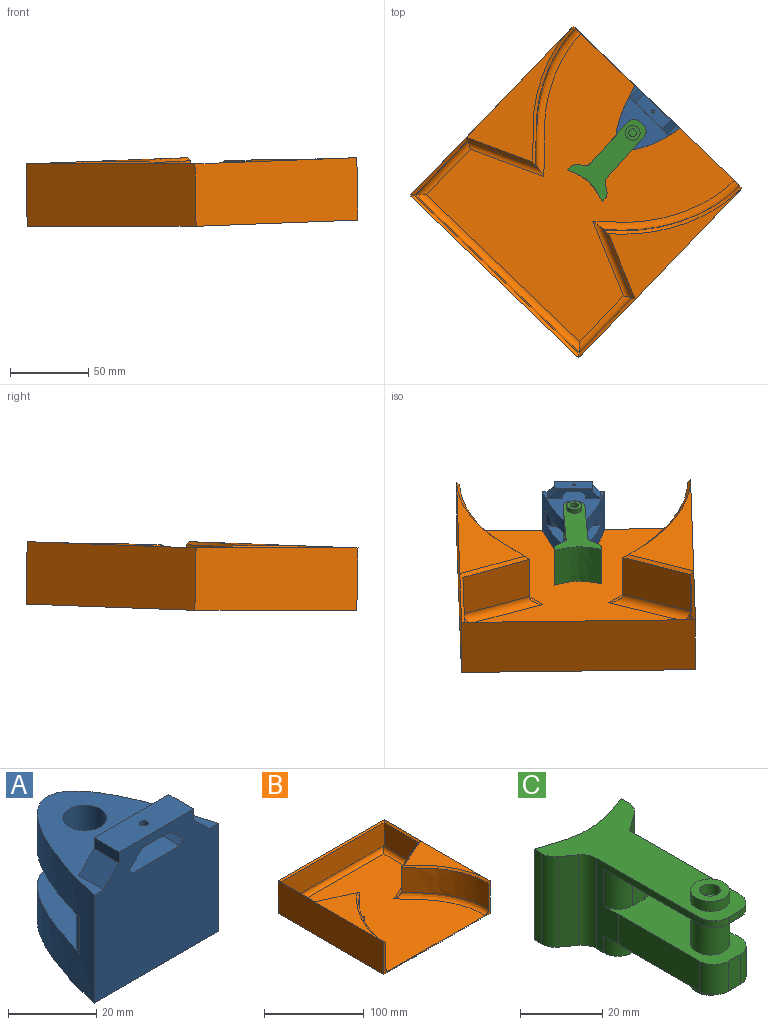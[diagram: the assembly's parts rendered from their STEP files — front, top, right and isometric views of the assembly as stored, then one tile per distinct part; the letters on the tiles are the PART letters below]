
ASSEMBLY  parts=3 mates=2
PART A: 24 faces, bbox 40x36.5x38 mm
  f0: plane 34x8mm, normal (0,1,0), area 140.4mm2, adj f1,f11,f12,f13,f14,f16,f17,f20
  f1: plane 40x36.51mm, normal (0,0,1), area 724.5mm2, adj f0,f2,f3,f10,f16,f17,f22,f23
  f2: extruded ~40x35mm, area 1821.4mm2, adj f1,f3,f4,f6,f7,f18,f19
  f3: plane 40x38mm, normal (0,-1,0), area 1340.4mm2, adj f1,f2,f4,f11,f12,f13,f14,f16
  f4: plane 40x36.51mm, normal (0,0,-1), area 955.1mm2, adj f2,f3
  f5: plane 26.97x10mm, normal (0,1,0), area 269.7mm2, adj f6,f7,f18,f19
  f6: plane 36.58x28.72mm, normal (0,0,-1), area 508.6mm2, adj f2,f5,f10,f18,f19
  f7: plane 36.58x28.72mm, normal (0,0,1), area 508.6mm2, adj f2,f5,f8,f18,f19
  f8: cylinder r=5mm len=10mm, axis (0,0,1), area 157.1mm2, adj f7,f9
  f9: cone r=0mm half-angle=59deg, axis (0,0,1), area 91.6mm2, adj f8
  f10: cylinder r=5mm len=10mm, axis (0,0,1), area 314.2mm2, adj f1,f6
  f11: plane 8x3mm, normal (-1,0,0), area 24mm2, adj f0,f3,f13,f23
  f12: plane 8x3mm, normal (1,0,0), area 24mm2, adj f0,f3,f13,f22
  f13: plane 24x8mm, normal (0,0,1), area 188.9mm2, adj f0,f3,f11,f12,f15
  f14: plane 9x8mm, normal (0,0,-1), area 68.9mm2, adj f0,f3,f15,f20,f21
  f15: cylinder r=1mm len=2.5mm, axis (0,0,1), area 15.7mm2, adj f13,f14
  f16: plane 8x1.25mm, normal (-0.71,0,0.71), area 14.1mm2, adj f0,f1,f3,f20
  f17: plane 8x1.25mm, normal (0.71,0,0.71), area 14.1mm2, adj f0,f1,f3,f21
  f18: cylinder r=5mm len=10mm, axis (0,0,-1), area 63.6mm2, adj f2,f5,f6,f7
  f19: cylinder r=5mm len=10mm, axis (0,0,-1), area 65.5mm2, adj f2,f5,f6,f7
  f20: plane 8x4.25mm, normal (-0.71,0,-0.71), area 48.1mm2, adj f0,f3,f14,f16
  f21: plane 8x4.25mm, normal (0.71,0,-0.71), area 48.1mm2, adj f0,f3,f14,f17
  f22: plane 8x5mm, normal (0.71,0,0.71), area 56.6mm2, adj f0,f1,f3,f12
  f23: plane 8x5mm, normal (-0.71,0,0.71), area 56.6mm2, adj f0,f1,f3,f11
PART B: 29 faces, bbox 152.7x155.3x42.7 mm
  f0: plane 100.52x44.36mm, normal (0,0,1), area 1461.1mm2, adj f2,f17,f19
  f1: extruded ~80.59x43mm, area 2909.3mm2, adj f5,f11,f17,f27,f28
  f2: plane 150x40mm, normal (1,0,0), area 6000mm2, adj f0,f3,f5,f13,f21
  f3: plane 150x40mm, normal (0,1,0), area 6000mm2, adj f2,f4,f13,f20
  f4: plane 150x40mm, normal (-1,0,0), area 6000mm2, adj f3,f5,f12,f13,f18
  f5: plane 150x40mm, normal (0,-1,0), area 312.7mm2, adj f1,f2,f4,f6,f13,f14,f15,f17
  f6: extruded ~79.99x43mm, area 2895.3mm2, adj f5,f7,f15,f22,f23
  f7: plane 43x29.74mm, normal (0.41,0.91,0), area 1387.6mm2, adj f6,f8,f16,f23
  f8: plane 48.91x29.36mm, normal (1,0,0), area 1403.8mm2, adj f7,f9,f18,f23,f24
  f9: plane 146x28.19mm, normal (0,-1,0), area 4115mm2, adj f8,f10,f20,f24,f25,f26
  f10: plane 48.86x29.35mm, normal (-1,0,0), area 1402.5mm2, adj f9,f11,f21,f26,f27
  f11: plane 43x29.73mm, normal (-0.4,0.92,0), area 1380.5mm2, adj f1,f10,f19,f27
  f12: plane 98.48x42.02mm, normal (0,0,1), area 1448.7mm2, adj f4,f15,f16
  f13: plane 150x150mm, normal (0,0,-1), area 22500mm2, adj f2,f3,f4,f5
  f14: plane 143.14x136mm, normal (0,-0.03,1), area 15961.1mm2, adj f5,f22,f23,f24,f25,f26,f27,f28
  f15: bspline ~87.22x48.6mm, area 262.9mm2, adj f5,f6,f12,f16
  f16: plane 45.01x19.68mm, normal (0.29,0.65,0.71), area 130.5mm2, adj f7,f12,f15,f18
  f17: bspline ~86.45x46.7mm, area 264.3mm2, adj f0,f1,f5,f19
  f18: plane 52.21x2mm, normal (0.71,0,0.71), area 143mm2, adj f4,f8,f16,f20
  f19: plane 45.14x19.43mm, normal (-0.28,0.65,0.71), area 130.4mm2, adj f0,f11,f17,f21
  f20: plane 150x2mm, normal (0,-0.71,0.71), area 418.6mm2, adj f3,f9,f18,f21
  f21: plane 52.18x2mm, normal (-0.71,0,0.71), area 142.9mm2, adj f2,f10,f19,f20
  f22: bspline ~126.16x98.33mm, area 740.9mm2, adj f5,f6,f14,f23
  f23: cylinder r=5mm len=52.2mm, axis (-0.91,0.41,0.01), area 388.5mm2, adj f6,f7,f8,f14,f22,f24
  f24: cylinder r=5mm len=49.04mm, axis (0,1,0.03), area 360.7mm2, adj f8,f9,f14,f23,f25
  f25: cylinder r=5mm len=146mm, axis (1,0,0), area 1088.6mm2, adj f9,f14,f24,f26
  f26: cylinder r=5mm len=48.99mm, axis (0,-1,-0.03), area 360.2mm2, adj f9,f10,f14,f25,f27
  f27: cylinder r=5mm len=51.26mm, axis (-0.92,-0.4,-0.01), area 383.7mm2, adj f1,f10,f11,f14,f26,f28
  f28: bspline ~99.94x62.69mm, area 743.7mm2, adj f1,f5,f14,f27
PART C: 39 faces, bbox 30.1x53.9x30 mm
  f0: plane 38.05x14.02mm, normal (0,0,-1), area 391.4mm2, adj f6,f8,f15,f16,f17,f18,f21,f27
  f1: plane 27x6.02mm, normal (0.59,-0.81,0), area 138mm2, adj f9,f11,f12,f19,f33,f38
  f2: plane 27x2.47mm, normal (1,0,0), area 66.6mm2, adj f3,f12,f19,f33
  f3: extruded ~30.11x27mm, area 838.6mm2, adj f2,f4,f12,f19
  f4: plane 27x2.46mm, normal (-1,0,0), area 66.3mm2, adj f3,f12,f19,f34
  f5: plane 27x3.98mm, normal (-0.59,-0.81,0), area 133.2mm2, adj f12,f19,f34,f35
  f6: plane 35.48x27mm, normal (-1,0,0), area 177.9mm2, adj f0,f12,f13,f14,f15,f19,f27,f31
  f7: plane 11x4mm, normal (0,-1,0), area 44mm2, adj f13,f14,f36,f37
  f8: plane 25x7.41mm, normal (1,0,0), area 105.3mm2, adj f0,f9,f14,f16,f19,f28,f37,f38
  f9: plane 6.88x2.05mm, normal (0,0,1), area 1mm2, adj f1,f8,f11,f37,f38
  f10: plane 3.87x2mm, normal (0,-1,0), area 7.7mm2, adj f12,f13,f31,f32
  f11: plane 37.97x2mm, normal (1,0,0), area 75.9mm2, adj f1,f9,f12,f13,f32
  f12: plane 53.9x30.12mm, normal (0,0,1), area 731.6mm2, adj f1,f2,f3,f4,f5,f6,f10,f11
  f13: plane 37.98x13.98mm, normal (0,0,-1), area 388.1mm2, adj f6,f7,f10,f11,f20,f31,f32,f36
  f14: plane 38.05x14.02mm, normal (0,0,1), area 391.4mm2, adj f6,f7,f8,f15,f16,f17,f20,f29
  f15: plane 28x9mm, normal (-1,0,0), area 252mm2, adj f0,f6,f14,f30
  f16: plane 28.05x9mm, normal (1,0,0), area 252.4mm2, adj f0,f8,f14,f29
  f17: plane 9x4mm, normal (0,-1,0), area 36mm2, adj f0,f14,f29,f30
  f18: plane 5x4mm, normal (0,-1,0), area 20mm2, adj f0,f19,f27,f28
  f19: plane 30.12x20.9mm, normal (0,0,-1), area 344.5mm2, adj f1,f2,f3,f4,f5,f6,f8,f18
  f20: cylinder r=4.75mm len=11mm, axis (0,0,1), area 328.3mm2, adj f13,f14
  f21: cylinder r=4.75mm len=9.5mm, axis (0,0,1), area 89.5mm2, adj f0,f22
  f22: plane 9.5x9.5mm, normal (0,0,-1), area 70.9mm2, adj f21
  f23: cylinder r=2.5mm len=5mm, axis (0,0,-1), area 47.1mm2, adj f25,f26
  f24: cylinder r=4.75mm len=9.5mm, axis (0,0,-1), area 89.5mm2, adj f12,f25
  f25: plane 9.5x9.5mm, normal (0,0,1), area 51.2mm2, adj f23,f24
  f26: plane 5x5mm, normal (0,0,1), area 19.6mm2, adj f23
  f27: cylinder r=5mm len=5.02mm, axis (0,0,-1), area 39.3mm2, adj f0,f6,f18,f19
  f28: cylinder r=5mm len=5.02mm, axis (0,0,-1), area 39.3mm2, adj f0,f8,f18,f19
  f29: cylinder r=5mm len=9mm, axis (0,0,1), area 70.7mm2, adj f0,f14,f16,f17
  f30: cylinder r=5mm len=9mm, axis (0,0,1), area 70.7mm2, adj f0,f14,f15,f17
  f31: cylinder r=5mm len=5.02mm, axis (0,0,-1), area 15.7mm2, adj f6,f10,f12,f13
  f32: cylinder r=5mm len=5mm, axis (0,0,-1), area 15.7mm2, adj f10,f11,f12,f13
  f33: cylinder r=5mm len=27mm, axis (0,0,1), area 126.6mm2, adj f1,f2,f12,f19
  f34: cylinder r=5mm len=27mm, axis (0,0,1), area 127mm2, adj f4,f5,f12,f19
  f35: cylinder r=5mm len=27mm, axis (0,0,-1), area 126.1mm2, adj f5,f6,f12,f19
  f36: cylinder r=5mm len=11mm, axis (0,0,1), area 86.4mm2, adj f6,f7,f13,f14
  f37: cylinder r=5mm len=11mm, axis (0,0,1), area 86.4mm2, adj f7,f8,f9,f13,f14
  f38: cylinder r=5mm len=25mm, axis (0,0,-1), area 117.6mm2, adj f1,f8,f9,f19
PLACE A rot(axis=(0,0,1),136.2deg) t=(-802.8,1500.65,-32.5)mm
PLACE B rot(axis=(-0.01,-0.01,1),136.2deg) t=(-802.91,1500.54,-20.05)mm
PLACE C rot(axis=(0,0,1),137.9deg) t=(-846.52,1476.52,-32.5)mm
MATE revolute A.f8 <-> C.f20  axis (0,0,1) through (0,0,-7.5)mm
MATE fastened A.f4 <-> B.f14  axis (0,0,-1) through (15.92,16.6,-32.5)mm
